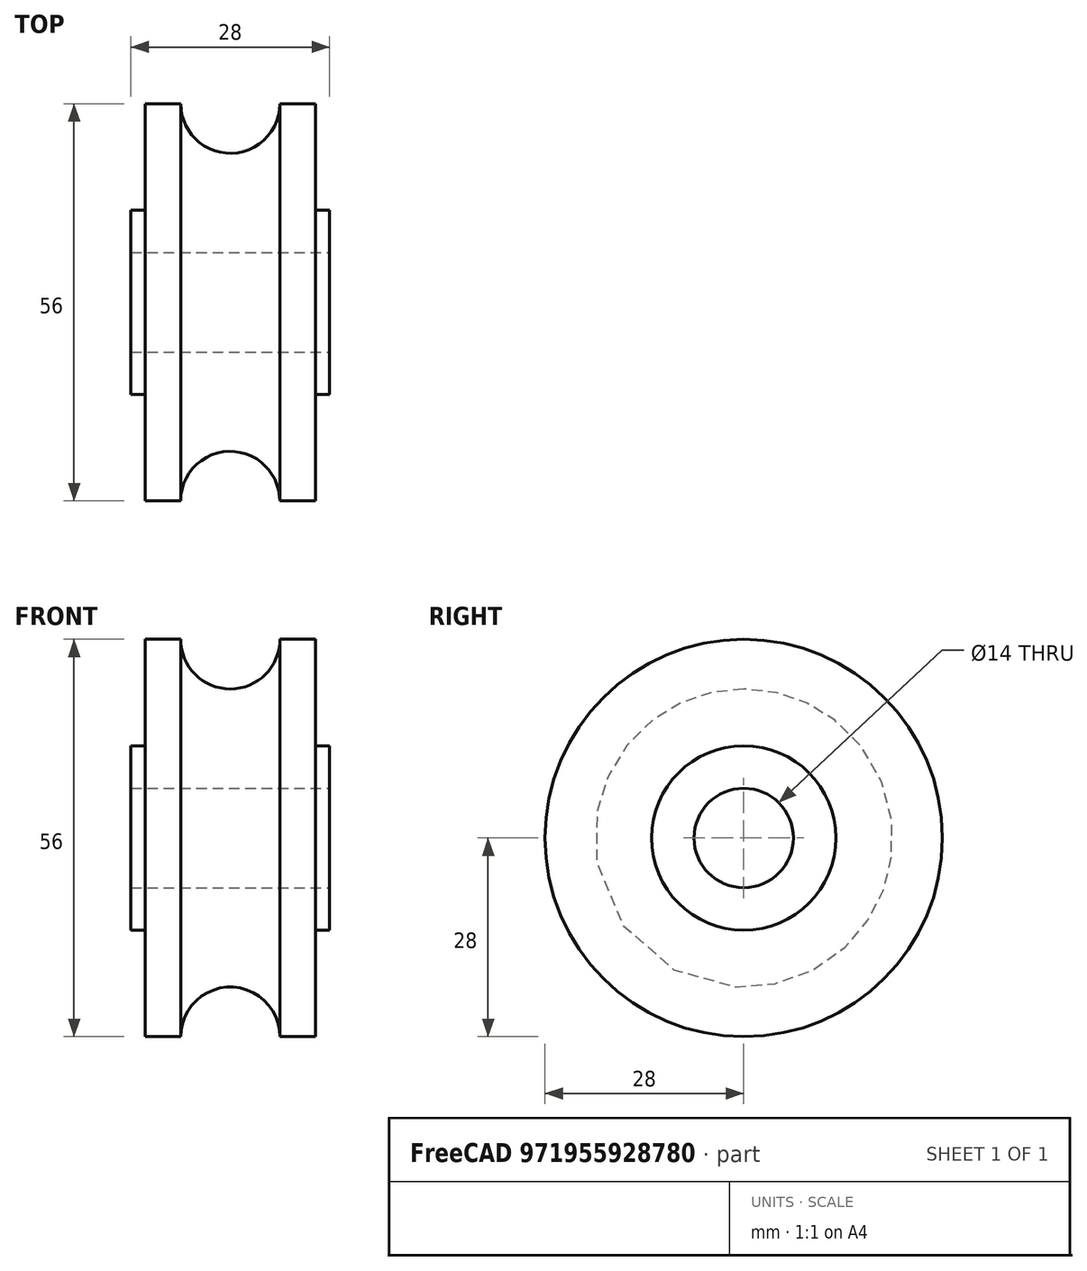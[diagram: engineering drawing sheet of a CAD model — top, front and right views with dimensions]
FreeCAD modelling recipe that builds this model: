
FCSTD DOCUMENT  (FreeCAD 0.21R33771 (Git))
Label: item_04_part_03
License: All rights reserved
LicenseURL: http://en.wikipedia.org/wiki/All_rights_reserved
objects: TechDraw::DrawViewDimension×7, TechDraw::DrawProjGroupItem×2, Sketcher::SketchObject×1, PartDesign::Revolution×1, PartDesign::Body×1, TechDraw::DrawSVGTemplate×1, TechDraw::DrawViewPart×1, TechDraw::DrawProjGroup×1, TechDraw::DrawPage×1
note: 12 computed .brp shape members not serialized (recipe doc carries the construction recipe); baked Part::Feature solids carry a one-line shape summary decoded from their .brp

FEATURE [Sketcher::SketchObject] Sketch
  FullyConstrained = true
  MapMode = 5
  Placement = pos=(0,0,0) rot=(1,0,0;1.5708rad)
  Support = -> [XZ_Plane]
  sketch-geometry (10):
    g0: LineSegment StartX=-14 StartY=7 StartZ=0 EndX=14 EndY=7 EndZ=0
    g1: LineSegment StartX=14 StartY=7 StartZ=0 EndX=14 EndY=13 EndZ=0
    g2: LineSegment StartX=14 StartY=13 StartZ=0 EndX=12 EndY=13 EndZ=0
    g3: LineSegment StartX=12 StartY=13 StartZ=0 EndX=12 EndY=28 EndZ=0
    g4: LineSegment StartX=12 StartY=28 StartZ=0 EndX=7 EndY=28 EndZ=0
    g5: ArcOfCircle CenterX=0 CenterY=28 CenterZ=0 NormalX=0 NormalY=0 NormalZ=1 AngleXU=0 Radius=7 StartAngle=3.14159 EndAngle=6.28319
    g6: LineSegment StartX=-7 StartY=28 StartZ=0 EndX=-12 EndY=28 EndZ=0
    g7: LineSegment StartX=-12 StartY=28 StartZ=0 EndX=-12 EndY=13 EndZ=0
    g8: LineSegment StartX=-12 StartY=13 StartZ=0 EndX=-14 EndY=13 EndZ=0
    g9: LineSegment StartX=-14 StartY=13 StartZ=0 EndX=-14 EndY=7 EndZ=0
  constraints (27):
    c: Horizontal(g0)
    c: Coincident(g0,g1)
    c: Vertical(g1)
    c: Coincident(g1,g2)
    c: Coincident(g2,g3)
    c: Coincident(g3,g4)
    c: Perpendicular(g4,g5) = 4.71239
    c: Perpendicular(g5,g6) = 4.71239
    c: Perpendicular(g6,g7) = 1.5708
    c: Perpendicular(g7,g8) = 4.71239
    c: Coincident(g8,g9)
    c: Coincident(g9,g0)
    c: Vertical(g9)
    c: Horizontal(g8)
    c: Horizontal(g2)
    c: Horizontal(g4)
    c: Vertical(g3)
    c: DistanceY(g9,g9) = 6
    c: Equal(g9,g1)
    c: Diameter(g5) = 14
    c: DistanceX(g6,g3) = 24
    c: Equal(g4,g6)
    c: DistanceX(g0,g0) = 28
    c: Equal(g8,g2)
    c: PointOnObject(g5,g-2)
    c: DistanceY(g-1,g6) = 28
    c: DistanceY(g3,g3) = 15
FEATURE [PartDesign::Revolution] Revolution
  Angle = 360
  Axis = (1,0,0)
  Base = (0,0,0)
  Placement = pos=(0,0,0) rot=(1,0,0;1.5708rad)
  Profile = -> Sketch
  ReferenceAxis = -> X_Axis
FEATURE [PartDesign::Body] Body
  Group = -> [Sketch,Revolution]
  Origin = -> Origin
  Tip = -> Revolution
FEATURE [TechDraw::DrawSVGTemplate] Template
  EditableTexts = Designed_by_Name=Reza Heshmati; Drawing_number=Drawing number; FC-Date=Date; FC-SC=Scale; FC-SH=Sheet; FC-Title=Item #4 (part 3); Subtitle=Subtitle; Weight=Weight
  Height = 210
  Orientation = 1
  Template = <path>
  Width = 297
FEATURE [TechDraw::DrawViewPart] View
  Caption = 3D View
  CoarseView = false
  Direction = (0.57735,-0.57735,0.57735)
  Focus = 100
  HardHidden = false
  IsoCount = 0
  IsoHidden = false
  IsoVisible = false
  LockPosition = false
  Perspective = false
  Rotation = 0
  ScaleType = 0
  ScrubCount = 0
  SeamHidden = false
  SeamVisible = false
  SmoothHidden = false
  SmoothVisible = true
  Source = -> [Revolution]
  X = 62.1048
  XDirection = (0.707107,0.707107,0)
  Y = 146.333
FEATURE [TechDraw::DrawProjGroupItem] ProjItem  label="Front"
  Caption = Front View
  CoarseView = false
  Direction = (0,-1,0)
  Focus = 100
  HardHidden = false
  IsoCount = 0
  IsoHidden = false
  IsoVisible = false
  LockPosition = true
  Perspective = false
  Rotation = 0
  RotationVector = (1,0,0)
  ScaleType = 2
  ScrubCount = 0
  SeamHidden = false
  SeamVisible = false
  SmoothHidden = false
  SmoothVisible = true
  Source = -> [Revolution]
  Type = 0
  X = 0
  XDirection = (1,0,0)
  Y = 0
FEATURE [TechDraw::DrawProjGroupItem] ProjItem001  label="Right"
  Caption = Side View
  CoarseView = false
  Direction = (1,-1e-16,0)
  Focus = 100
  HardHidden = false
  IsoCount = 0
  IsoHidden = false
  IsoVisible = false
  LockPosition = false
  Perspective = false
  Rotation = 0
  RotationVector = (1,0,0)
  ScaleType = 2
  ScrubCount = 0
  SeamHidden = false
  SeamVisible = false
  SmoothHidden = false
  SmoothVisible = true
  Source = -> [Revolution]
  Type = 2
  X = -57
  XDirection = (1e-16,1,0)
  Y = 0
FEATURE [TechDraw::DrawProjGroup] ProjGroup
  Anchor = -> ProjItem
  AutoDistribute = true
  LockPosition = false
  ProjectionType = 0
  Rotation = 0
  ScaleType = 0
  Source = -> [Revolution]
  Views = -> [ProjItem,ProjItem001]
  X = 229.151
  Y = 115.349
  spacingX = 15
  spacingY = 15
FEATURE [TechDraw::DrawViewDimension] Dimension
  AngleOverride = false
  Arbitrary = false
  ArbitraryTolerances = false
  EqualTolerance = true
  ExtensionAngle = 0
  FormatSpec = ⌀%.2w
  FormatSpecOverTolerance = %+.2w
  FormatSpecUnderTolerance = %+.2w
  Inverted = false
  LineAngle = 0
  LockPosition = false
  MeasureType = 1
  OverTolerance = 0
  References2D = -> [ProjItem001]
  Rotation = 0
  ScaleType = 0
  TheoreticalExact = false
  Type = 5
  UnderTolerance = 0
  X = 11.4844
  Y = 40.0552
FEATURE [TechDraw::DrawViewDimension] Dimension001
  AngleOverride = false
  Arbitrary = false
  ArbitraryTolerances = false
  EqualTolerance = true
  ExtensionAngle = 0
  FormatSpec = ⌀%.2w
  FormatSpecOverTolerance = %+.2w
  FormatSpecUnderTolerance = %+.2w
  Inverted = false
  LineAngle = 0
  LockPosition = false
  MeasureType = 1
  OverTolerance = 0
  References2D = -> [ProjItem001]
  Rotation = 0
  ScaleType = 0
  TheoreticalExact = false
  Type = 5
  UnderTolerance = 0
  X = 16.2462
  Y = 17.6467
FEATURE [TechDraw::DrawViewDimension] Dimension002
  AngleOverride = false
  Arbitrary = false
  ArbitraryTolerances = false
  EqualTolerance = true
  ExtensionAngle = 0
  FormatSpec = ⌀%.2w
  FormatSpecOverTolerance = %+.2w
  FormatSpecUnderTolerance = %+.2w
  Inverted = false
  LineAngle = 0
  LockPosition = false
  MeasureType = 1
  OverTolerance = 0
  References2D = -> [ProjItem001]
  Rotation = 0
  ScaleType = 0
  TheoreticalExact = false
  Type = 5
  UnderTolerance = 0
  X = 17.3666
  Y = 1.68064
FEATURE [TechDraw::DrawViewDimension] Dimension003
  AngleOverride = false
  Arbitrary = false
  ArbitraryTolerances = false
  EqualTolerance = true
  ExtensionAngle = 0
  FormatSpec = %.2w
  FormatSpecOverTolerance = %+.2w
  FormatSpecUnderTolerance = %+.2w
  Inverted = false
  LineAngle = 0
  LockPosition = false
  MeasureType = 1
  OverTolerance = 0
  References2D = -> [ProjItem]
  Rotation = 0
  ScaleType = 0
  TheoreticalExact = false
  Type = 1
  UnderTolerance = 0
  X = -17.2995
  Y = 23.6299
FEATURE [TechDraw::DrawViewDimension] Dimension004
  AngleOverride = false
  Arbitrary = false
  ArbitraryTolerances = false
  EqualTolerance = true
  ExtensionAngle = 0
  FormatSpec = %.2w
  FormatSpecOverTolerance = %+.2w
  FormatSpecUnderTolerance = %+.2w
  Inverted = false
  LineAngle = 0
  LockPosition = false
  MeasureType = 1
  OverTolerance = 0
  References2D = -> [ProjItem]
  Rotation = 0
  ScaleType = 0
  TheoreticalExact = false
  Type = 1
  UnderTolerance = 0
  X = -9.69085
  Y = 43.8596
FEATURE [TechDraw::DrawViewDimension] Dimension005
  AngleOverride = false
  Arbitrary = false
  ArbitraryTolerances = false
  EqualTolerance = true
  ExtensionAngle = 0
  FormatSpec = ⌀%.2w
  FormatSpecOverTolerance = %+.2w
  FormatSpecUnderTolerance = %+.2w
  Inverted = false
  LineAngle = 0
  LockPosition = false
  MeasureType = 1
  OverTolerance = 0
  References2D = -> [ProjItem]
  Rotation = 0
  ScaleType = 0
  TheoreticalExact = false
  Type = 5
  UnderTolerance = 0
  X = 10.4968
  Y = 45.0408
FEATURE [TechDraw::DrawViewDimension] Dimension006
  AngleOverride = false
  Arbitrary = false
  ArbitraryTolerances = false
  EqualTolerance = true
  ExtensionAngle = 0
  FormatSpec = %.2w
  FormatSpecOverTolerance = %+.2w
  FormatSpecUnderTolerance = %+.2w
  Inverted = false
  LineAngle = 0
  LockPosition = false
  MeasureType = 1
  OverTolerance = 0
  References2D = -> [ProjItem]
  Rotation = 0
  ScaleType = 0
  TheoreticalExact = false
  Type = 1
  UnderTolerance = 0
  X = 0.381702
  Y = -9.57871
FEATURE [TechDraw::DrawPage] Page
  KeepUpdated = true
  NextBalloonIndex = 1
  ProjectionType = 0
  Template = -> Template
  Views = -> [View,ProjGroup,Dimension,Dimension001,Dimension002,Dimension003,Dimension004,Dimension005,Dimension006]
note: 1 file-system path scrubbed to <path> (originals preserved in the JSON sidecar)
